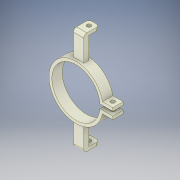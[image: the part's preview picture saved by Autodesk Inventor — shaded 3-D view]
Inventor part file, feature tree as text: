
AUTODESK INVENTOR PART (.ipt)
format: ipt  version: 2019 (Build 230136000, 136)  size: 184,832 bytes
history: native  units: mm
features: extrude x5, sketch x5, plane x3, fillet x1, mirror x1, projected_geometry x1
ambient origin geometry x8: Origin, YZ Plane, XZ Plane, XY Plane, X Axis, Y Axis, Z Axis, Center Point
bodies: Solid1 (feature_tree)
feature tree (16):
  extrude  "Extrusion1"  Depth=52.0mm
  extrude  "Extrusion2"  Depth=10.0mm TaperAngle=0.0deg
  plane  "Work Plane3"
  extrude  "Extrusion3"  Depth=10.0mm TaperAngle=0.0deg
  plane  "Work Plane4"
  extrude  "Extrusion4"  Depth=4.0mm TaperAngle=0.0deg
  plane  "Work Plane2"
  extrude  "Extrusion5"  Depth=10.0mm
  fillet  "Fillet2"  Radius=4.0mm
  mirror  "Mirror3"
  sketch  "Sketch1"  dims[d0=46.5mm d1=52.0mm]
  sketch  "Sketch2"  dims[d10=10.0mm d11=0.0mm d13=11.0mm d14=0.0mm]
  sketch  "Sketch3"  dims[d19=22.5mm d20=0.0mm d23=10.0mm d24=0.0mm]
  sketch  "Sketch4"  dims[d29=4.0mm d30=4.0mm d31=0.0mm]
  sketch  "Sketch5"  dims[d33=3.0mm d34=10.0mm d35=4.0mm d36=15.0mm d37=3.0mm d38=3.0mm]
  projected_geometry  "Projected Loop2"
